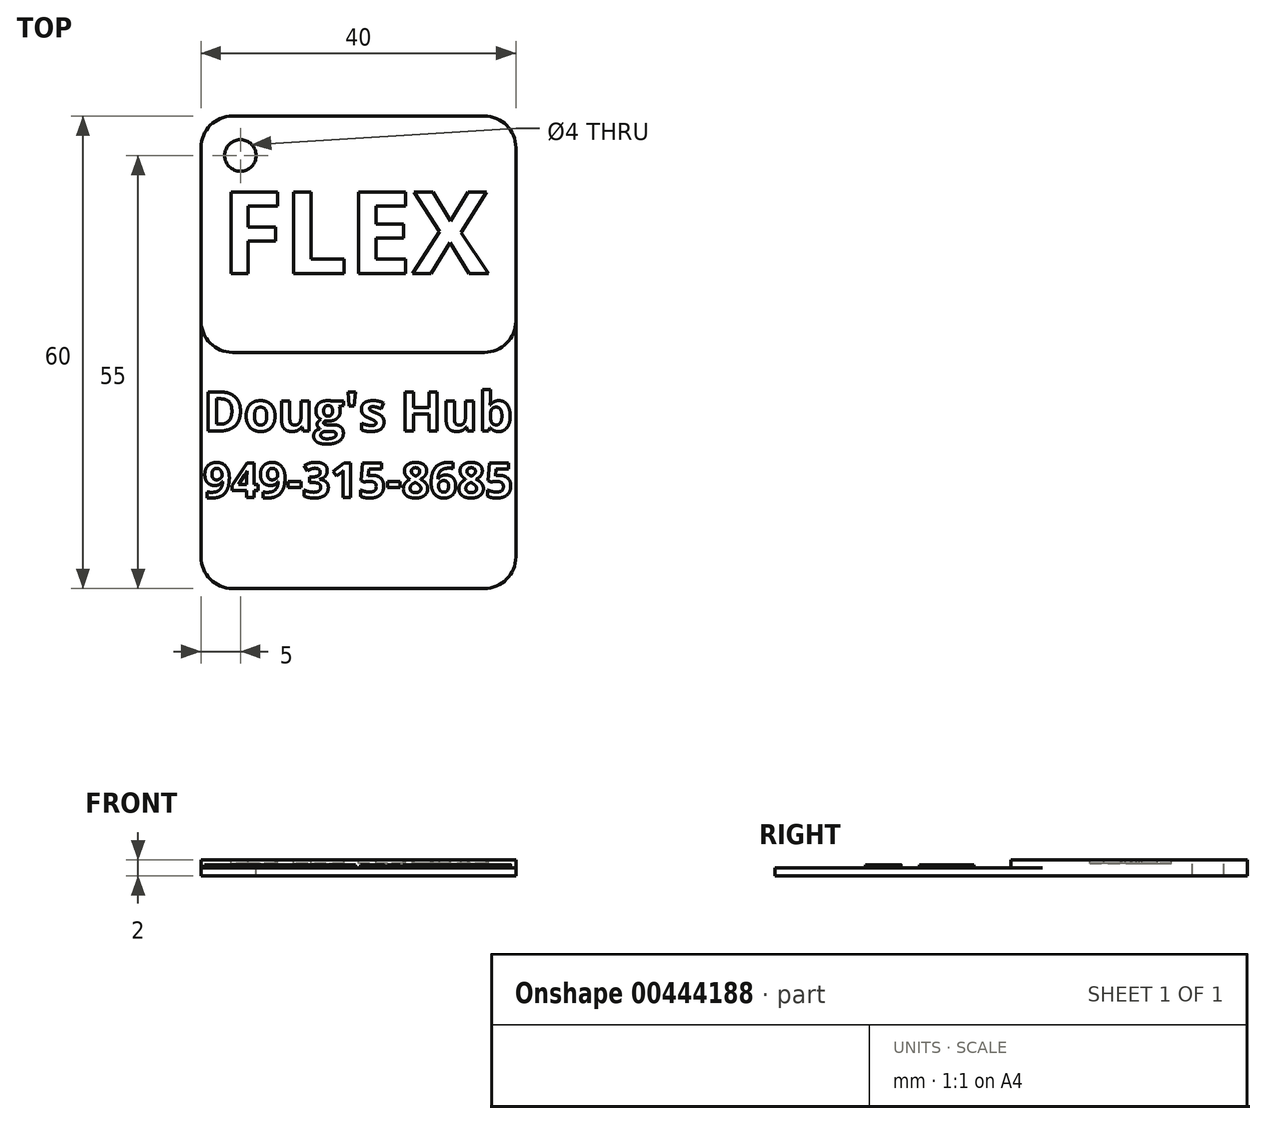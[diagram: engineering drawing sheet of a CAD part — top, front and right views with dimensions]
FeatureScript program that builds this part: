
annotation { "Feature Type Name" : "Feature", "Feature Type Description" : "" }
export const myFeature = defineFeature(function(context is Context, id is Id, definition is map)
    precondition{}
    {
        {
            var Q0;
            Q0=qCreatedBy(makeId("Top.planeOp"),FACE);
            var sketch = newSketch(context, id + "F0", { "sketchPlane" : qUnion([Q0])});
            skLineSegment(sketch, "E0.bottom", {"start": v(0, 0) * mm, "end": v(40, 0) * mm});
            skLineSegment(sketch, "E0.top", {"start": v(0, 60) * mm, "end": v(40, 60) * mm});
            skLineSegment(sketch, "E0.left", {"start": v(0, 0) * mm, "end": v(0, 60) * mm});
            skLineSegment(sketch, "E0.right", {"start": v(40, 0) * mm, "end": v(40, 60) * mm});
            skSolve(sketch);
        }
        {
            var Q0;
            Q0=qSketchRegion(id+"F0",true);
            extrude(context, id + "F1", {"entities" : qUnion([Q0]), "depth" : 1 * mm});
        }
        {
            var Q0;
            Q0=makeQuery(id+"F1.opExtrude","CAP_FACE",FACE,{"disambiguationData":[OSD([sQuery(id+"F0.wireOp",EDGE,"E0.bottom"),sQuery(id+"F0.wireOp",EDGE,"E0.top"),sQuery(id+"F0.wireOp",EDGE,"E0.left"),sQuery(id+"F0.wireOp",EDGE,"E0.right")])],"isStart":false});
            var sketch = newSketch(context, id + "F2", { "sketchPlane" : qUnion([Q0])});
            skLineSegment(sketch, "E1.bottom", {"start": v(0, 60) * mm, "end": v(40, 60) * mm});
            skLineSegment(sketch, "E1.top", {"start": v(0, 30) * mm, "end": v(40, 30) * mm});
            skLineSegment(sketch, "E1.left", {"start": v(0, 60) * mm, "end": v(0, 30) * mm});
            skLineSegment(sketch, "E1.right", {"start": v(40, 60) * mm, "end": v(40, 30) * mm});
            skSolve(sketch);
        }
        {
            var Q0;
            Q0=qSketchRegion(id+"F2",true);
            extrude(context, id + "F3", {"entities" : qUnion([Q0]), "operationType" : NewBodyOperationType.ADD, "depth" : 1 * mm});
        }
        {
            var Q0;
            Q0=makeQuery(id+"F1.opExtrude","CAP_FACE",FACE,{"disambiguationData":[OSD([sQuery(id+"F0.wireOp",EDGE,"E0.bottom"),sQuery(id+"F0.wireOp",EDGE,"E0.top"),sQuery(id+"F0.wireOp",EDGE,"E0.left"),sQuery(id+"F0.wireOp",EDGE,"E0.right")])],"isStart":false});
            var sketch = newSketch(context, id + "F4", { "sketchPlane" : qUnion([Q0])});
            skPoint(sketch, "E2.oppositeSnap0", {"position": v(20, 25) * mm});
            skLineSegment(sketch, "E2.bottom", {"start": v(24.97, 0) * mm, "end": v(24.97, 0) * mm});
            skText(sketch, "E3", { "text": "Doug\'s Hub", "fontName": "OpenSans-Bold.ttf"});
            skText(sketch, "E4", { "text": "949-315-8685", "fontName": "OpenSans-Bold.ttf"});
            const initialGuessF4  = {"E3": [0.00028, 0.02, 1, 0, 0.005], "E4": [0.00028, 0.01154, 1, 0, 0.00446]};
            skSetInitialGuess(sketch, initialGuessF4);
            skSolve(sketch);
        }
        {
            var Q0;
            Q0=qSketchRegion(id+"F4",true);
            extrude(context, id + "F5", {"entities" : qUnion([Q0]), "operationType" : NewBodyOperationType.ADD, "depth" : .4 * mm});
        }
        {
            var Q0;
            Q0=makeQuery(id+"F3.opExtrude","CAP_FACE",FACE,{"disambiguationData":[OSD([sQuery(id+"F2.wireOp",EDGE,"E1.bottom"),sQuery(id+"F2.wireOp",EDGE,"E1.top"),sQuery(id+"F2.wireOp",EDGE,"E1.left"),sQuery(id+"F2.wireOp",EDGE,"E1.right")])],"isStart":false});
            var sketch = newSketch(context, id + "F6", { "sketchPlane" : qUnion([Q0])});
            skText(sketch, "E5", { "text": "FLEX", "fontName": "OpenSans-Bold.ttf"});
            const initialGuessF6  = {"E5": [0.0025, 0.04, 1, 0, 0.01047]};
            skSetInitialGuess(sketch, initialGuessF6);
            skSolve(sketch);
        }
        {
            var Q0;
            Q0=qSketchRegion(id+"F6",true);
            extrude(context, id + "F7", {"entities" : qUnion([Q0]), "operationType" : NewBodyOperationType.REMOVE, "oppositeDirection" : true, "depth" : .4 * mm});
        }
        {
            var Q0;
            {var subQ0=sQuery(id+"F2.wireOp",EDGE,"E1.left");var subQ1=sQuery(id+"F2.wireOp",EDGE,"E1.top");var subQ2=sQuery(id+"F2.wireOp",EDGE,"E1.bottom");var subQ3=sQuery(id+"F2.wireOp",EDGE,"E1.right");Q0=makeQuery(id+"F7.boolean.opBoolean","SPLIT",FACE,{"disambiguationData":[TD([makeQuery(id+"F1.opExtrude","SWEPT_FACE",FACE,{"disambiguationData":[OSD([sQuery(id+"F0.wireOp",EDGE,"E0.top")])]})])],"derivedFrom":makeQuery(id+"F3.opExtrude","CAP_FACE",FACE,{"disambiguationData":[OSD([subQ2,subQ1,subQ0,subQ3])],"isStart":false})});}
            var sketch = newSketch(context, id + "F8", { "sketchPlane" : qUnion([Q0])});
            skCircle(sketch, "E6", {"center": v(5, 55) * mm, "radius": 2 * mm});
            skSolve(sketch);
        }
        {
            var Q0;
            Q0=qSketchRegion(id+"F8",true);
            extrude(context, id + "F9", {"entities" : qUnion([Q0]), "operationType" : NewBodyOperationType.REMOVE, "endBound" : BoundingType.THROUGH_ALL, "oppositeDirection" : true, "depth" : 25.4 * mm});
        }
        {
            var Q0;
            Q0=makeQuery(id+"F3.opExtrude","SWEPT_EDGE",EDGE,{"disambiguationData":[OSD([sQuery(id+"F0.wireOp",EDGE,"E0.left"),sQuery(id+"F2.wireOp",EDGE,"E1.top"),sQuery(id+"F2.wireOp",EDGE,"E1.left")])]});
            var Q1;
            Q1=makeQuery(id+"F3.opExtrude","SWEPT_EDGE",EDGE,{"disambiguationData":[OSD([sQuery(id+"F0.wireOp",EDGE,"E0.right"),sQuery(id+"F2.wireOp",EDGE,"E1.top"),sQuery(id+"F2.wireOp",EDGE,"E1.right")])]});
            var Q2;
            Q2=makeQuery(id+"F1.opExtrude","SWEPT_EDGE",EDGE,{"disambiguationData":[OSD([sQuery(id+"F0.wireOp",EDGE,"E0.bottom"),sQuery(id+"F0.wireOp",EDGE,"E0.left")])]});
            var Q3;
            Q3=makeQuery(id+"F1.opExtrude","SWEPT_EDGE",EDGE,{"disambiguationData":[OSD([sQuery(id+"F0.wireOp",EDGE,"E0.bottom"),sQuery(id+"F0.wireOp",EDGE,"E0.right")])]});
            var Q4;
            Q4=makeQuery(id+"F3.boolean.opBoolean","MERGE",EDGE,{"derivedFrom":[makeQuery(id+"F1.opExtrude","SWEPT_EDGE",EDGE,{"disambiguationData":[OSD([sQuery(id+"F0.wireOp",EDGE,"E0.top"),sQuery(id+"F0.wireOp",EDGE,"E0.right")])]}),makeQuery(id+"F3.opExtrude","SWEPT_EDGE",EDGE,{"disambiguationData":[OSD([sQuery(id+"F2.wireOp",EDGE,"E1.bottom"),sQuery(id+"F2.wireOp",EDGE,"E1.right")])]})]});
            var Q5;
            Q5=makeQuery(id+"F3.boolean.opBoolean","MERGE",EDGE,{"derivedFrom":[makeQuery(id+"F1.opExtrude","SWEPT_EDGE",EDGE,{"disambiguationData":[OSD([sQuery(id+"F0.wireOp",EDGE,"E0.top"),sQuery(id+"F0.wireOp",EDGE,"E0.left")])]}),makeQuery(id+"F3.opExtrude","SWEPT_EDGE",EDGE,{"disambiguationData":[OSD([sQuery(id+"F2.wireOp",EDGE,"E1.bottom"),sQuery(id+"F2.wireOp",EDGE,"E1.left")])]})]});
            fillet(context, id + "F10", {"entities" : qUnion([Q0, Q1, Q2, Q3, Q4, Q5]), "radius" : 4 * mm, "tangentPropagation" : true, "allowEdgeOverflow" : false});
        }
    });
